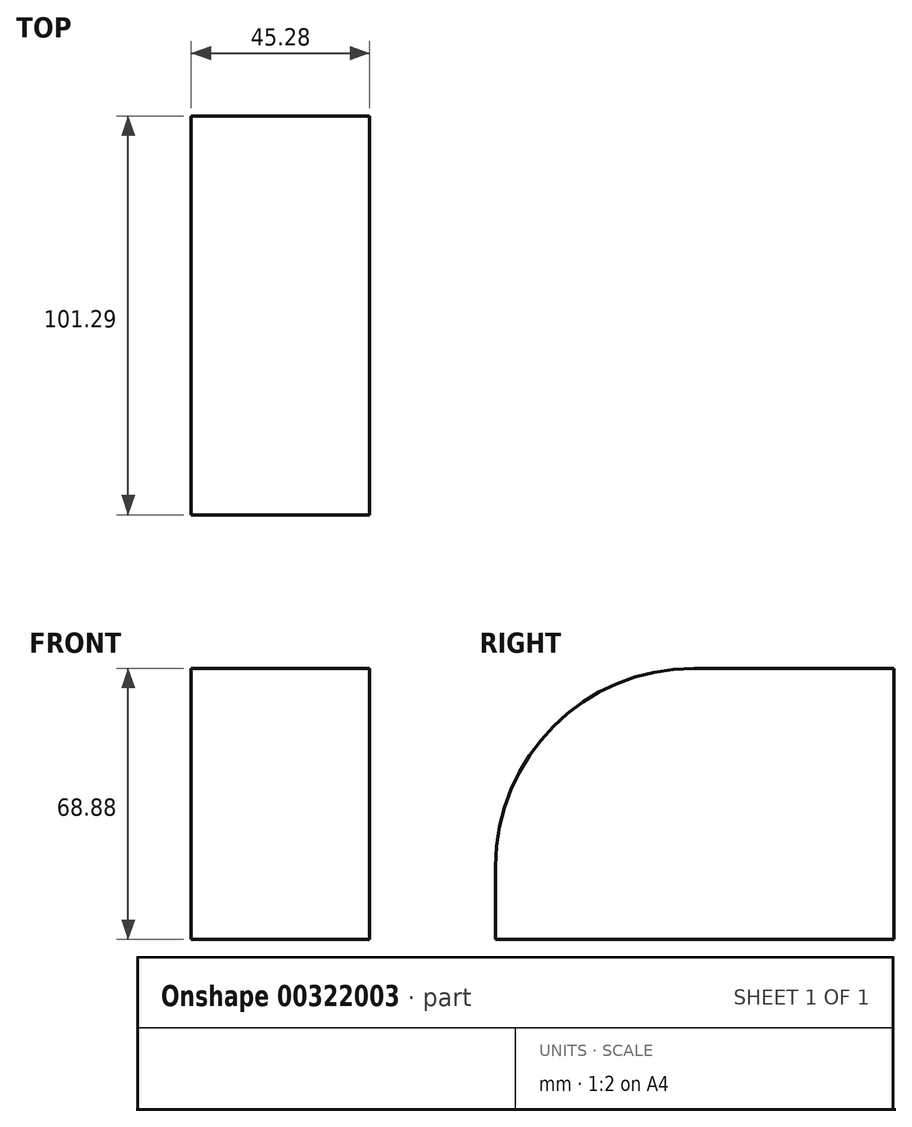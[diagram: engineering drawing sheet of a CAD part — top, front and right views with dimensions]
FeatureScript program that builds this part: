
annotation { "Feature Type Name" : "Feature", "Feature Type Description" : "" }
export const myFeature = defineFeature(function(context is Context, id is Id, definition is map)
    precondition{}
    {
        {
            var Q0;
            Q0=qCreatedBy(makeId("Right.planeOp"),FACE);
            var sketch = newSketch(context, id + "F0", { "sketchPlane" : qUnion([Q0])});
            skLineSegment(sketch, "E0.bottom", {"start": v(-36.56, -34.44) * mm, "end": v(64.73, -34.44) * mm});
            skLineSegment(sketch, "E0.top", {"start": v(-36.56, 34.44) * mm, "end": v(64.73, 34.44) * mm});
            skLineSegment(sketch, "E0.left", {"start": v(-36.56, -34.44) * mm, "end": v(-36.56, 34.44) * mm});
            skLineSegment(sketch, "E0.right", {"start": v(64.73, -34.44) * mm, "end": v(64.73, 34.44) * mm});
            skPoint(sketch, "E0.middle", {"position": v(14.09, 0) * mm});
            skSolve(sketch);
        }
        {
            var Q0;
            Q0=makeQuery(id+"F0.imprint","IMPRINT",FACE,{"disambiguationData":[TD([[makeQuery(id+"F0.imprint","IMPRINT",EDGE,{"derivedFrom":sQuery(id+"F0.wireOp",EDGE,"E0.bottom")}),1.0]])]});
            extrude(context, id + "F1", {"entities" : qUnion([Q0]), "depth" : 45.28 * mm});
        }
        {
            var Q0;
            Q0=makeQuery(id+"F1.opExtrude","SWEPT_EDGE",EDGE,{"disambiguationData":[OSD([sQuery(id+"F0.wireOp",EDGE,"E0.top"),sQuery(id+"F0.wireOp",EDGE,"E0.left")])]});
            fillet(context, id + "F2", {"entities" : qUnion([Q0]), "radius" : 50.36 * mm, "tangentPropagation" : true, "allowEdgeOverflow" : false});
        }
    });
